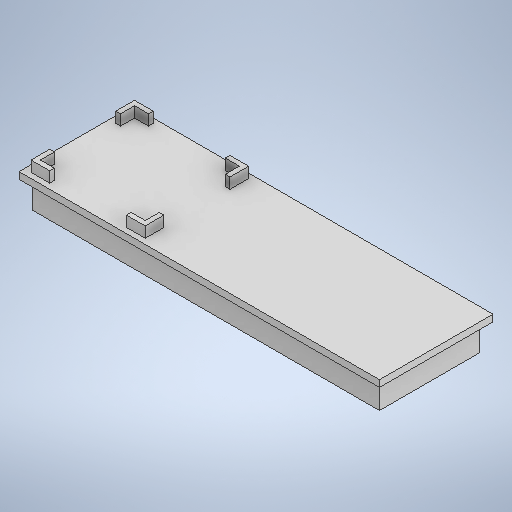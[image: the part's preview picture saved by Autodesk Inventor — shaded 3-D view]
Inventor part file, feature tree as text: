
AUTODESK INVENTOR PART (.ipt)
format: ipt  version: 2025 (Build 290162010, 162A)  size: 428,544 bytes
history: native  units: in
note: dims shown in document units (in); Inventor stores cm internally (conversion verified against a paired STEP export)
features: move_body x8, sketch x7, direct_edit x6, extrude x5, mirror x3
ambient origin geometry x8: Origin, YZ Plane, XZ Plane, XY Plane, X Axis, Y Axis, Z Axis, Center Point
bodies: Solid1 (feature_tree)
feature tree (29):
  extrude  "Extrusion1"  Depth=5.1181in
  sketch  "Sketch2"  dims[d2=0.1378in d3=0.1378in]
  extrude  "Extrusion2"  Depth=0.1378in
  extrude  "Extrusion3"  Depth=0.1378in
  mirror  "Mirror1"
  direct_edit  "Direct Edit1"
  sketch  "Sketch5"  dims[d9=0.0443in d10=0.2953in d11=0.0in]
  sketch  "Sketch6"  dims[d12=1.3386in]
  extrude  "Extrusion4"  Depth=0.0344in
  mirror  "Mirror2"
  extrude  "Extrusion5"  Depth=0.2953in TaperAngle=0.0deg
  mirror  "Mirror3"
  direct_edit  "Direct Edit2"
  direct_edit  "Direct Edit3"
  direct_edit  "Direct Edit4"
  direct_edit  "Direct Edit5"
  direct_edit  "Direct Edit6"
  sketch  "Sketch1"  dims[d0=1.4764in d1=5.1181in]
  sketch  "Sketch3"  dims[d4=0.1378in d5=0.1378in]
  sketch  "Sketch4"  dims[d6=0.0984in d7=0.0in d8=0.0344in]
  sketch  "Sketch7"  dims[d13=1.4961in d14=1.4764in d15=0.0689in d16=0.0689in d17=0.0689in d18=0.2756in d19=0.2756in d20=0.2756in d21=0.2756in d22=0.1575in d23=0.0in d24=0.0in d25=0.0in d26=0.0984in d27=0.0984in d28=0.0984in d29=0.0in d30=0.0984in d31=0.0in d32=0.0in d33=-0.0394in d34=0.0in d35=0.0in d36=-0.0394in d37=0.0in d38=0.0394in d39=0.0in d40=0.0in d41=0.0394in d42=0.0in d43=0.0in d44=-0.0295in d45=0.0in d46=0.0in d47=0.0in d48=0.0in d49=-0.0098in d50=0.0in d51=0.0197in d52=0.0in]
  move_body  "Move1"
  move_body  "Move2"
  move_body  "Move3"
  move_body  "Move4"
  move_body  "Move5"
  move_body  "Move6"
  move_body  "Move7"
  move_body  "Move8"
